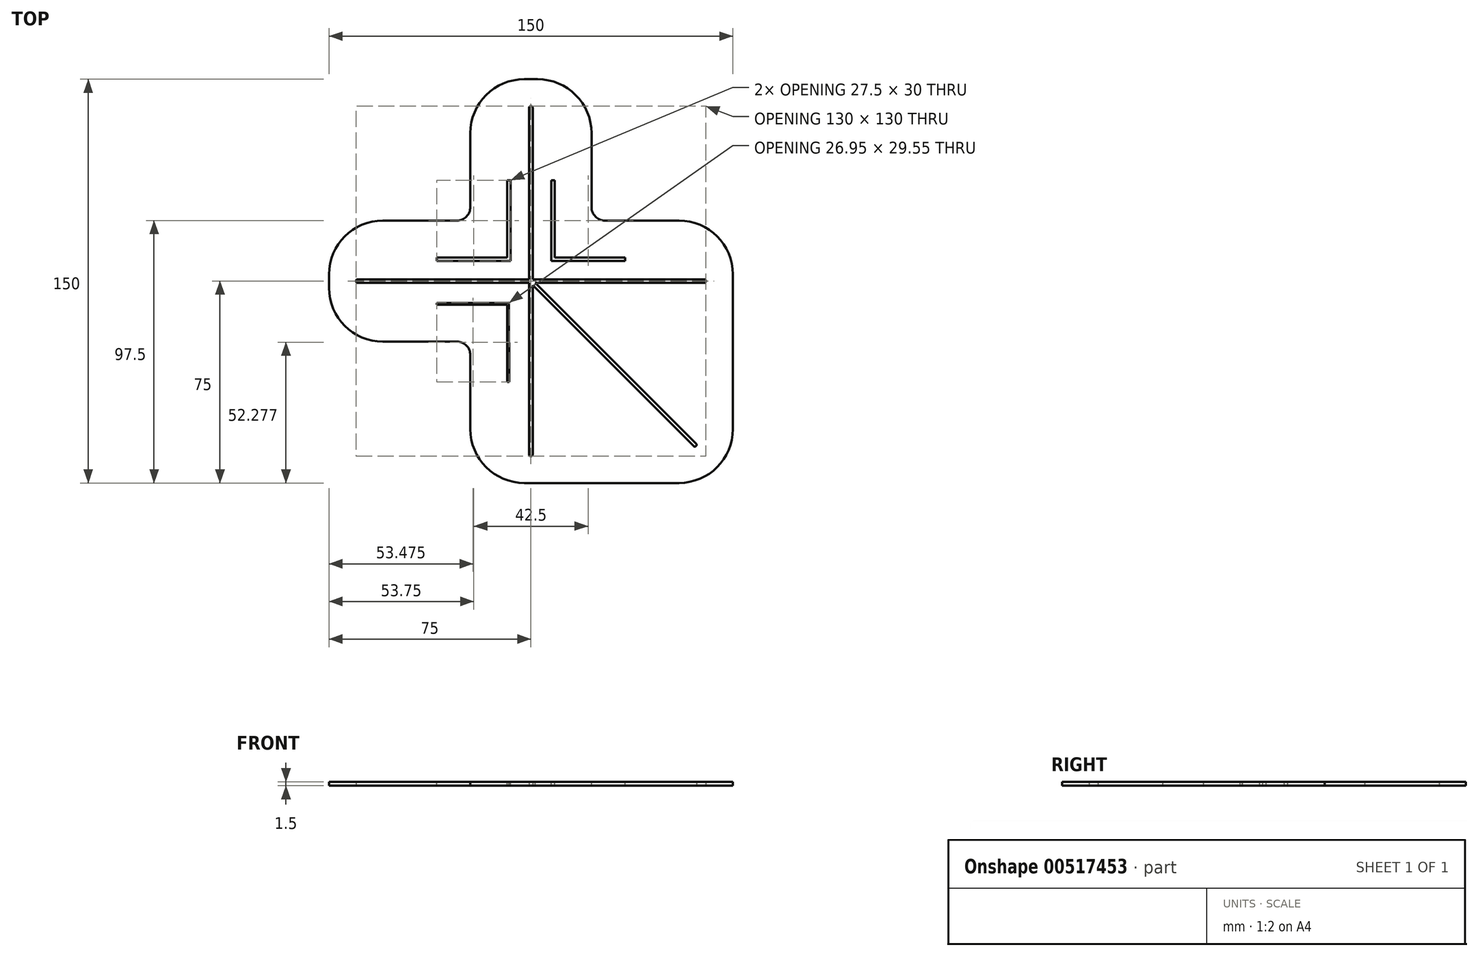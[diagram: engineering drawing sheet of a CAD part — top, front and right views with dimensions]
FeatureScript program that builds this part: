
annotation { "Feature Type Name" : "Feature", "Feature Type Description" : "" }
export const myFeature = defineFeature(function(context is Context, id is Id, definition is map)
    precondition{}
    {
        {
            var Q0;
            Q0=qCreatedBy(makeId("Top.planeOp"),FACE);
            var sketch = newSketch(context, id + "F0", { "sketchPlane" : qUnion([Q0])});
            skLineSegment(sketch, "E0.bottom", {"start": v(75, 75) * mm, "end": v(-75, 75) * mm});
            skLineSegment(sketch, "E0.top", {"start": v(75, -75) * mm, "end": v(-75, -75) * mm});
            skLineSegment(sketch, "E0.left", {"start": v(75, 75) * mm, "end": v(75, -75) * mm});
            skLineSegment(sketch, "E0.right", {"start": v(-75, 75) * mm, "end": v(-75, -75) * mm});
            skPoint(sketch, "E0.middle", {"position": v(0, 0) * mm});
            skLineSegment(sketch, "E1.bottom", {"start": v(0.65, -65) * mm, "end": v(-0.65, -65) * mm});
            skLineSegment(sketch, "E1.top", {"start": v(0.65, 65) * mm, "end": v(-0.65, 65) * mm});
            skLineSegment(sketch, "E1.left", {"start": v(0.65, -65) * mm, "end": v(0.65, -0.65) * mm});
            skLineSegment(sketch, "E1.right", {"start": v(-0.65, -65) * mm, "end": v(-0.65, -0.65) * mm});
            skLineSegment(sketch, "E2.bottom", {"start": v(-65, -0.65) * mm, "end": v(-0.65, -0.65) * mm});
            skLineSegment(sketch, "E2.top", {"start": v(-65, 0.65) * mm, "end": v(-0.65, 0.65) * mm});
            skLineSegment(sketch, "E2.left", {"start": v(-65, -0.65) * mm, "end": v(-65, 0.65) * mm});
            skLineSegment(sketch, "E2.right", {"start": v(65, -0.65) * mm, "end": v(65, 0.65) * mm});
            skLineSegment(sketch, "E3.trimOffspring", {"start": v(0.65, 0.65) * mm, "end": v(0.65, 65) * mm});
            skLineSegment(sketch, "E4.trimOffspring", {"start": v(0.65, 0.65) * mm, "end": v(65, 0.65) * mm});
            skLineSegment(sketch, "E5.trimOffspring", {"start": v(-0.65, 0.65) * mm, "end": v(-0.65, 65) * mm});
            skLineSegment(sketch, "E6.trimOffspring", {"start": v(0.65, -0.65) * mm, "end": v(65, -0.65) * mm});
            skSolve(sketch);
        }
        {
            var Q0;
            Q0 = qSketchRegion(id + "F0", true);
            extrude(context, id + "F1", {"entities" : qUnion([Q0]), "depth" : 1.5 * mm, "offsetDistance" : 25 * mm});
        }
        {
            var Q0;
            Q0=makeQuery(id+"F1.opExtrude","CAP_FACE",FACE,{"disambiguationData":[OSD([sQuery(id+"F0.wireOp",EDGE,"E0.bottom"),sQuery(id+"F0.wireOp",EDGE,"E0.top"),sQuery(id+"F0.wireOp",EDGE,"E0.left"),sQuery(id+"F0.wireOp",EDGE,"E0.right"),sQuery(id+"F0.wireOp",EDGE,"E1.bottom"),sQuery(id+"F0.wireOp",EDGE,"E1.top"),sQuery(id+"F0.wireOp",EDGE,"E1.left"),sQuery(id+"F0.wireOp",EDGE,"E1.right"),sQuery(id+"F0.wireOp",EDGE,"E2.bottom"),sQuery(id+"F0.wireOp",EDGE,"E2.top"),sQuery(id+"F0.wireOp",EDGE,"E2.left"),sQuery(id+"F0.wireOp",EDGE,"E2.right"),sQuery(id+"F0.wireOp",EDGE,"E3.trimOffspring"),sQuery(id+"F0.wireOp",EDGE,"E4.trimOffspring"),sQuery(id+"F0.wireOp",EDGE,"E5.trimOffspring"),sQuery(id+"F0.wireOp",EDGE,"E6.trimOffspring")])],"isStart":false});
            var sketch = newSketch(context, id + "F2", { "sketchPlane" : qUnion([Q0])});
            skLineSegment(sketch, "E7.0", {"start": v(0.46, 0.46) * mm, "end": v(61.74, -60.82) * mm});
            skLineSegment(sketch, "E8.0", {"start": v(-0.46, -0.46) * mm, "end": v(60.82, -61.74) * mm});
            skLineSegment(sketch, "E9", {"start": v(0.46, 0.46) * mm, "end": v(-0.46, -0.46) * mm});
            skLineSegment(sketch, "E10", {"start": v(61.74, -60.82) * mm, "end": v(60.82, -61.74) * mm});
            skSolve(sketch);
        }
        {
            var Q0;
            Q0 = qSketchRegion(id + "F2", true);
            extrude(context, id + "F3", {"entities" : qUnion([Q0]), "operationType" : NewBodyOperationType.REMOVE, "oppositeDirection" : true, "depth" : 25 * mm, "offsetDistance" : 25 * mm});
        }
        {
            var Q0;
            Q0=makeQuery(id+"F1.opExtrude","SWEPT_EDGE",EDGE,{"disambiguationData":[OSD([sQuery(id+"F0.wireOp",EDGE,"E1.bottom"),sQuery(id+"F0.wireOp",EDGE,"E1.left")])]});
            var Q1;
            Q1=makeQuery(id+"F1.opExtrude","SWEPT_EDGE",EDGE,{"disambiguationData":[OSD([sQuery(id+"F0.wireOp",EDGE,"E1.bottom"),sQuery(id+"F0.wireOp",EDGE,"E1.right")])]});
            var Q2;
            Q2=makeQuery(id+"F3.boolean.opBoolean","COPY",EDGE,{"derivedFrom":makeQuery(id+"F3.opExtrude","SWEPT_EDGE",EDGE,{"disambiguationData":[OSD([sQuery(id+"F2.wireOp",EDGE,"E8.0"),sQuery(id+"F2.wireOp",EDGE,"E10")])]})});
            var Q3;
            Q3=makeQuery(id+"F3.boolean.opBoolean","COPY",EDGE,{"derivedFrom":makeQuery(id+"F3.opExtrude","SWEPT_EDGE",EDGE,{"disambiguationData":[OSD([sQuery(id+"F2.wireOp",EDGE,"E7.0"),sQuery(id+"F2.wireOp",EDGE,"E10")])]})});
            var Q4;
            Q4=makeQuery(id+"F1.opExtrude","SWEPT_EDGE",EDGE,{"disambiguationData":[OSD([sQuery(id+"F0.wireOp",EDGE,"E2.right"),sQuery(id+"F0.wireOp",EDGE,"E4.trimOffspring")])]});
            var Q5;
            Q5=makeQuery(id+"F1.opExtrude","SWEPT_EDGE",EDGE,{"disambiguationData":[OSD([sQuery(id+"F0.wireOp",EDGE,"E2.right"),sQuery(id+"F0.wireOp",EDGE,"E6.trimOffspring")])]});
            var Q6;
            Q6=makeQuery(id+"F1.opExtrude","SWEPT_EDGE",EDGE,{"disambiguationData":[OSD([sQuery(id+"F0.wireOp",EDGE,"E2.bottom"),sQuery(id+"F0.wireOp",EDGE,"E2.left")])]});
            var Q7;
            Q7=makeQuery(id+"F1.opExtrude","SWEPT_EDGE",EDGE,{"disambiguationData":[OSD([sQuery(id+"F0.wireOp",EDGE,"E2.top"),sQuery(id+"F0.wireOp",EDGE,"E2.left")])]});
            var Q8;
            Q8=makeQuery(id+"F1.opExtrude","SWEPT_EDGE",EDGE,{"disambiguationData":[OSD([sQuery(id+"F0.wireOp",EDGE,"E1.top"),sQuery(id+"F0.wireOp",EDGE,"E5.trimOffspring")])]});
            var Q9;
            Q9=makeQuery(id+"F1.opExtrude","SWEPT_EDGE",EDGE,{"disambiguationData":[OSD([sQuery(id+"F0.wireOp",EDGE,"E1.top"),sQuery(id+"F0.wireOp",EDGE,"E3.trimOffspring")])]});
            fillet(context, id + "F4", {"entities" : qUnion([Q0, Q1, Q2, Q3, Q4, Q5, Q6, Q7, Q8, Q9]), "radius" : .5 * mm, "tangentPropagation" : true, "allowEdgeOverflow" : false});
        }
        {
            var Q0;
            Q0=makeQuery(id+"F1.opExtrude","CAP_FACE",FACE,{"disambiguationData":[OSD([sQuery(id+"F0.wireOp",EDGE,"E0.bottom"),sQuery(id+"F0.wireOp",EDGE,"E0.top"),sQuery(id+"F0.wireOp",EDGE,"E0.left"),sQuery(id+"F0.wireOp",EDGE,"E0.right"),sQuery(id+"F0.wireOp",EDGE,"E1.bottom"),sQuery(id+"F0.wireOp",EDGE,"E1.top"),sQuery(id+"F0.wireOp",EDGE,"E1.left"),sQuery(id+"F0.wireOp",EDGE,"E1.right"),sQuery(id+"F0.wireOp",EDGE,"E2.bottom"),sQuery(id+"F0.wireOp",EDGE,"E2.top"),sQuery(id+"F0.wireOp",EDGE,"E2.left"),sQuery(id+"F0.wireOp",EDGE,"E2.right"),sQuery(id+"F0.wireOp",EDGE,"E3.trimOffspring"),sQuery(id+"F0.wireOp",EDGE,"E4.trimOffspring"),sQuery(id+"F0.wireOp",EDGE,"E5.trimOffspring"),sQuery(id+"F0.wireOp",EDGE,"E6.trimOffspring")])],"isStart":false});
            var sketch = newSketch(context, id + "F5", { "sketchPlane" : qUnion([Q0])});
            skLineSegment(sketch, "E11.bottom", {"start": v(-7.5, 7.5) * mm, "end": v(7.5, 7.5) * mm, "construction": true});
            skLineSegment(sketch, "E11.top", {"start": v(-7.5, -7.5) * mm, "end": v(7.5, -7.5) * mm, "construction": true});
            skLineSegment(sketch, "E11.left", {"start": v(-7.5, 7.5) * mm, "end": v(-7.5, -7.5) * mm, "construction": true});
            skLineSegment(sketch, "E11.right", {"start": v(7.5, 7.5) * mm, "end": v(7.5, -7.5) * mm, "construction": true});
            skPoint(sketch, "E11.middle", {"position": v(0, 0) * mm});
            skLineSegment(sketch, "E12.top", {"start": v(-7.5, 37.5) * mm, "end": v(-8.6, 37.5) * mm});
            skLineSegment(sketch, "E12.left", {"start": v(-7.5, 7.5) * mm, "end": v(-7.5, 37.5) * mm});
            skLineSegment(sketch, "E12.right", {"start": v(-8.6, 8.6) * mm, "end": v(-8.6, 37.5) * mm});
            skLineSegment(sketch, "E13.bottom", {"start": v(-8.6, 7.5) * mm, "end": v(-35, 7.5) * mm});
            skLineSegment(sketch, "E13.top", {"start": v(-8.6, 8.6) * mm, "end": v(-35, 8.6) * mm});
            skLineSegment(sketch, "E13.right", {"start": v(-35, 7.5) * mm, "end": v(-35, 8.6) * mm});
            skCircle(sketch, "E14", {"center": v(0, 0) * mm, "radius": 18.96 * mm, "construction": true});
            skLineSegment(sketch, "E15", {"start": v(-8.6, 7.5) * mm, "end": v(-7.5, 7.5) * mm});
            skPoint(sketch, "E16.center", {"position": v(0, 8.75) * mm});
            skLineSegment(sketch, "E17", {"start": v(0, 75) * mm, "end": v(0, -60.5) * mm, "construction": true});
            skLineSegment(sketch, "E18", {"start": v(75, 0.15) * mm, "end": v(37.58, 0) * mm, "construction": true});
            skLineSegment(sketch, "E19.MirrorCS", {"start": v(8.6, 7.5) * mm, "end": v(7.5, 7.5) * mm});
            skLineSegment(sketch, "E20.MirrorCS", {"start": v(7.5, 37.5) * mm, "end": v(8.6, 37.5) * mm});
            skLineSegment(sketch, "E21.MirrorCS", {"start": v(35, 7.5) * mm, "end": v(35, 8.6) * mm});
            skLineSegment(sketch, "E22.MirrorCS", {"start": v(8.6, 8.6) * mm, "end": v(8.6, 37.5) * mm});
            skLineSegment(sketch, "E23.MirrorCS", {"start": v(8.6, 7.5) * mm, "end": v(35, 7.5) * mm});
            skLineSegment(sketch, "E24.MirrorCS", {"start": v(7.5, 7.5) * mm, "end": v(7.5, 37.5) * mm});
            skLineSegment(sketch, "E25.MirrorCS", {"start": v(8.6, 8.6) * mm, "end": v(35, 8.6) * mm});
            skLineSegment(sketch, "E26.MirrorCS", {"start": v(7.5, 7.5) * mm, "end": v(-7.5, 7.5) * mm, "construction": true});
            skSolve(sketch);
        }
        {
            var Q0;
            Q0 = qSketchRegion(id + "F5", true);
            extrude(context, id + "F6", {"entities" : qUnion([Q0]), "operationType" : NewBodyOperationType.REMOVE, "oppositeDirection" : true, "depth" : 25 * mm, "offsetDistance" : 25 * mm});
        }
        {
            var Q0;
            Q0=makeQuery(id+"F1.opExtrude","CAP_FACE",FACE,{"disambiguationData":[OSD([sQuery(id+"F0.wireOp",EDGE,"E0.bottom"),sQuery(id+"F0.wireOp",EDGE,"E0.top"),sQuery(id+"F0.wireOp",EDGE,"E0.left"),sQuery(id+"F0.wireOp",EDGE,"E0.right"),sQuery(id+"F0.wireOp",EDGE,"E1.bottom"),sQuery(id+"F0.wireOp",EDGE,"E1.top"),sQuery(id+"F0.wireOp",EDGE,"E1.left"),sQuery(id+"F0.wireOp",EDGE,"E1.right"),sQuery(id+"F0.wireOp",EDGE,"E2.bottom"),sQuery(id+"F0.wireOp",EDGE,"E2.top"),sQuery(id+"F0.wireOp",EDGE,"E2.left"),sQuery(id+"F0.wireOp",EDGE,"E2.right"),sQuery(id+"F0.wireOp",EDGE,"E3.trimOffspring"),sQuery(id+"F0.wireOp",EDGE,"E4.trimOffspring"),sQuery(id+"F0.wireOp",EDGE,"E5.trimOffspring"),sQuery(id+"F0.wireOp",EDGE,"E6.trimOffspring")])],"isStart":false});
            var sketch = newSketch(context, id + "F7", { "sketchPlane" : qUnion([Q0])});
            skLineSegment(sketch, "E27.bottom", {"start": v(-22.5, -22.5) * mm, "end": v(-127.5, -22.5) * mm});
            skLineSegment(sketch, "E27.top", {"start": v(-22.5, -127.5) * mm, "end": v(-127.5, -127.5) * mm});
            skLineSegment(sketch, "E27.left", {"start": v(-22.5, -22.5) * mm, "end": v(-22.5, -127.5) * mm});
            skLineSegment(sketch, "E27.right", {"start": v(-127.5, -22.5) * mm, "end": v(-127.5, -127.5) * mm});
            skPoint(sketch, "E27.middle", {"position": v(-75, -75) * mm});
            skLineSegment(sketch, "E28.bottom", {"start": v(-22.5, 22.5) * mm, "end": v(-127.5, 22.5) * mm});
            skLineSegment(sketch, "E28.top", {"start": v(-22.5, 127.5) * mm, "end": v(-127.5, 127.5) * mm});
            skLineSegment(sketch, "E28.left", {"start": v(-22.5, 22.5) * mm, "end": v(-22.5, 127.5) * mm});
            skLineSegment(sketch, "E28.right", {"start": v(-127.5, 22.5) * mm, "end": v(-127.5, 127.5) * mm});
            skPoint(sketch, "E28.middle", {"position": v(-75, 75) * mm});
            skLineSegment(sketch, "E29.bottom", {"start": v(22.5, 22.5) * mm, "end": v(127.5, 22.5) * mm});
            skLineSegment(sketch, "E29.top", {"start": v(22.5, 127.5) * mm, "end": v(127.5, 127.5) * mm});
            skLineSegment(sketch, "E29.left", {"start": v(22.5, 22.5) * mm, "end": v(22.5, 127.5) * mm});
            skLineSegment(sketch, "E29.right", {"start": v(127.5, 22.5) * mm, "end": v(127.5, 127.5) * mm});
            skPoint(sketch, "E29.middle", {"position": v(75, 75) * mm});
            skSolve(sketch);
        }
        {
            var Q0;
            Q0 = qSketchRegion(id + "F7", true);
            extrude(context, id + "F8", {"entities" : qUnion([Q0]), "operationType" : NewBodyOperationType.REMOVE, "oppositeDirection" : true, "depth" : 25 * mm, "offsetDistance" : 25 * mm});
        }
        {
            var Q0;
            Q0=makeQuery(id+"F8.boolean.opBoolean","INTERSECT",EDGE,{"derivedFrom":[makeQuery(id+"F1.opExtrude","SWEPT_FACE",FACE,{"disambiguationData":[OSD([sQuery(id+"F0.wireOp",EDGE,"E0.right")])]}),makeQuery(id+"F8.opExtrude","SWEPT_FACE",FACE,{"disambiguationData":[OSD([sQuery(id+"F7.wireOp",EDGE,"E27.bottom")])]})]});
            var Q1;
            Q1=makeQuery(id+"F8.boolean.opBoolean","INTERSECT",EDGE,{"derivedFrom":[makeQuery(id+"F1.opExtrude","SWEPT_FACE",FACE,{"disambiguationData":[OSD([sQuery(id+"F0.wireOp",EDGE,"E0.top")])]}),makeQuery(id+"F8.opExtrude","SWEPT_FACE",FACE,{"disambiguationData":[OSD([sQuery(id+"F7.wireOp",EDGE,"E27.left")])]})]});
            var Q2;
            Q2=makeQuery(id+"F1.opExtrude","SWEPT_EDGE",EDGE,{"disambiguationData":[OSD([sQuery(id+"F0.wireOp",EDGE,"E0.top"),sQuery(id+"F0.wireOp",EDGE,"E0.left")])]});
            var Q3;
            Q3=makeQuery(id+"F8.boolean.opBoolean","INTERSECT",EDGE,{"derivedFrom":[makeQuery(id+"F1.opExtrude","SWEPT_FACE",FACE,{"disambiguationData":[OSD([sQuery(id+"F0.wireOp",EDGE,"E0.left")])]}),makeQuery(id+"F8.opExtrude","SWEPT_FACE",FACE,{"disambiguationData":[OSD([sQuery(id+"F7.wireOp",EDGE,"E29.bottom")])]})]});
            var Q4;
            Q4=makeQuery(id+"F8.boolean.opBoolean","INTERSECT",EDGE,{"derivedFrom":[makeQuery(id+"F1.opExtrude","SWEPT_FACE",FACE,{"disambiguationData":[OSD([sQuery(id+"F0.wireOp",EDGE,"E0.bottom")])]}),makeQuery(id+"F8.opExtrude","SWEPT_FACE",FACE,{"disambiguationData":[OSD([sQuery(id+"F7.wireOp",EDGE,"E29.left")])]})]});
            var Q5;
            Q5=makeQuery(id+"F8.boolean.opBoolean","INTERSECT",EDGE,{"derivedFrom":[makeQuery(id+"F1.opExtrude","SWEPT_FACE",FACE,{"disambiguationData":[OSD([sQuery(id+"F0.wireOp",EDGE,"E0.bottom")])]}),makeQuery(id+"F8.opExtrude","SWEPT_FACE",FACE,{"disambiguationData":[OSD([sQuery(id+"F7.wireOp",EDGE,"E28.left")])]})]});
            var Q6;
            Q6=makeQuery(id+"F8.boolean.opBoolean","INTERSECT",EDGE,{"derivedFrom":[makeQuery(id+"F1.opExtrude","SWEPT_FACE",FACE,{"disambiguationData":[OSD([sQuery(id+"F0.wireOp",EDGE,"E0.right")])]}),makeQuery(id+"F8.opExtrude","SWEPT_FACE",FACE,{"disambiguationData":[OSD([sQuery(id+"F7.wireOp",EDGE,"E28.bottom")])]})]});
            fillet(context, id + "F9", {"entities" : qUnion([Q0, Q1, Q2, Q3, Q4, Q5, Q6]), "radius" : 20 * mm, "tangentPropagation" : true, "allowEdgeOverflow" : false});
        }
        {
            var Q0;
            Q0=makeQuery(id+"F8.boolean.opBoolean","COPY",EDGE,{"derivedFrom":makeQuery(id+"F8.opExtrude","SWEPT_EDGE",EDGE,{"disambiguationData":[OSD([sQuery(id+"F7.wireOp",EDGE,"E27.bottom"),sQuery(id+"F7.wireOp",EDGE,"E27.left")])]})});
            var Q1;
            Q1=makeQuery(id+"F8.boolean.opBoolean","COPY",EDGE,{"derivedFrom":makeQuery(id+"F8.opExtrude","SWEPT_EDGE",EDGE,{"disambiguationData":[OSD([sQuery(id+"F7.wireOp",EDGE,"E28.bottom"),sQuery(id+"F7.wireOp",EDGE,"E28.left")])]})});
            var Q2;
            Q2=makeQuery(id+"F8.boolean.opBoolean","COPY",EDGE,{"derivedFrom":makeQuery(id+"F8.opExtrude","SWEPT_EDGE",EDGE,{"disambiguationData":[OSD([sQuery(id+"F7.wireOp",EDGE,"E29.bottom"),sQuery(id+"F7.wireOp",EDGE,"E29.left")])]})});
            fillet(context, id + "F10", {"entities" : qUnion([Q0, Q1, Q2]), "radius" : 5 * mm, "tangentPropagation" : true, "allowEdgeOverflow" : false});
        }
        {
            var Q0;
            Q0=makeQuery(id+"F1.opExtrude","CAP_FACE",FACE,{"disambiguationData":[OSD([sQuery(id+"F0.wireOp",EDGE,"E0.bottom"),sQuery(id+"F0.wireOp",EDGE,"E0.top"),sQuery(id+"F0.wireOp",EDGE,"E0.left"),sQuery(id+"F0.wireOp",EDGE,"E0.right"),sQuery(id+"F0.wireOp",EDGE,"E1.bottom"),sQuery(id+"F0.wireOp",EDGE,"E1.top"),sQuery(id+"F0.wireOp",EDGE,"E1.left"),sQuery(id+"F0.wireOp",EDGE,"E1.right"),sQuery(id+"F0.wireOp",EDGE,"E2.bottom"),sQuery(id+"F0.wireOp",EDGE,"E2.top"),sQuery(id+"F0.wireOp",EDGE,"E2.left"),sQuery(id+"F0.wireOp",EDGE,"E2.right"),sQuery(id+"F0.wireOp",EDGE,"E3.trimOffspring"),sQuery(id+"F0.wireOp",EDGE,"E4.trimOffspring"),sQuery(id+"F0.wireOp",EDGE,"E5.trimOffspring"),sQuery(id+"F0.wireOp",EDGE,"E6.trimOffspring")])],"isStart":false});
            var sketch = newSketch(context, id + "F11", { "sketchPlane" : qUnion([Q0])});
            skLineSegment(sketch, "E30", {"start": v(8.42, -7.5) * mm, "end": v(9.52, -8.6) * mm});
            skLineSegment(sketch, "E31", {"start": v(9.52, -8.6) * mm, "end": v(37.29, -9.78) * mm});
            skLineSegment(sketch, "E32", {"start": v(37.29, -9.78) * mm, "end": v(36.06, -4.77) * mm});
            skLineSegment(sketch, "E33", {"start": v(36.06, -4.77) * mm, "end": v(8.42, -7.5) * mm});
            skLineSegment(sketch, "E34", {"start": v(7.5, -8.42) * mm, "end": v(8.6, -9.52) * mm});
            skLineSegment(sketch, "E35", {"start": v(8.6, -9.52) * mm, "end": v(14.81, -40.76) * mm});
            skLineSegment(sketch, "E36", {"start": v(14.81, -40.76) * mm, "end": v(3.89, -40.76) * mm});
            skLineSegment(sketch, "E37", {"start": v(3.89, -40.76) * mm, "end": v(7.5, -8.42) * mm});
            skSolve(sketch);
        }
        {
            var Q0;
            Q0 = qSketchRegion(id + "F11", true);
            var Q1;
            Q1=makeQuery(id+"F1.opExtrude","CAP_FACE",FACE,{"disambiguationData":[OSD([sQuery(id+"F0.wireOp",EDGE,"E0.bottom"),sQuery(id+"F0.wireOp",EDGE,"E0.top"),sQuery(id+"F0.wireOp",EDGE,"E0.left"),sQuery(id+"F0.wireOp",EDGE,"E0.right"),sQuery(id+"F0.wireOp",EDGE,"E1.bottom"),sQuery(id+"F0.wireOp",EDGE,"E1.top"),sQuery(id+"F0.wireOp",EDGE,"E1.left"),sQuery(id+"F0.wireOp",EDGE,"E1.right"),sQuery(id+"F0.wireOp",EDGE,"E2.bottom"),sQuery(id+"F0.wireOp",EDGE,"E2.top"),sQuery(id+"F0.wireOp",EDGE,"E2.left"),sQuery(id+"F0.wireOp",EDGE,"E2.right"),sQuery(id+"F0.wireOp",EDGE,"E3.trimOffspring"),sQuery(id+"F0.wireOp",EDGE,"E4.trimOffspring"),sQuery(id+"F0.wireOp",EDGE,"E5.trimOffspring"),sQuery(id+"F0.wireOp",EDGE,"E6.trimOffspring")])],"isStart":true});
            extrude(context, id + "F12", {"entities" : qUnion([Q0]), "operationType" : NewBodyOperationType.ADD, "endBound" : BoundingType.UP_TO_SURFACE, "oppositeDirection" : true, "depth" : 15 * mm, "endBoundEntityFace" : qUnion([Q1]), "offsetDistance" : 25 * mm});
        }
        {
            var Q0;
            Q0=makeQuery(id+"F12.boolean.opBoolean","MERGE",FACE,{"derivedFrom":[makeQuery(id+"F1.opExtrude","CAP_FACE",FACE,{"disambiguationData":[OSD([sQuery(id+"F0.wireOp",EDGE,"E0.bottom"),sQuery(id+"F0.wireOp",EDGE,"E0.top"),sQuery(id+"F0.wireOp",EDGE,"E0.left"),sQuery(id+"F0.wireOp",EDGE,"E0.right"),sQuery(id+"F0.wireOp",EDGE,"E1.bottom"),sQuery(id+"F0.wireOp",EDGE,"E1.top"),sQuery(id+"F0.wireOp",EDGE,"E1.left"),sQuery(id+"F0.wireOp",EDGE,"E1.right"),sQuery(id+"F0.wireOp",EDGE,"E2.bottom"),sQuery(id+"F0.wireOp",EDGE,"E2.top"),sQuery(id+"F0.wireOp",EDGE,"E2.left"),sQuery(id+"F0.wireOp",EDGE,"E2.right"),sQuery(id+"F0.wireOp",EDGE,"E3.trimOffspring"),sQuery(id+"F0.wireOp",EDGE,"E4.trimOffspring"),sQuery(id+"F0.wireOp",EDGE,"E5.trimOffspring"),sQuery(id+"F0.wireOp",EDGE,"E6.trimOffspring")])],"isStart":false}),makeQuery(id+"F12.opExtrude","CAP_FACE",FACE,{"disambiguationData":[OSD([sQuery(id+"F11.wireOp",EDGE,"E30"),sQuery(id+"F11.wireOp",EDGE,"E31"),sQuery(id+"F11.wireOp",EDGE,"E32"),sQuery(id+"F11.wireOp",EDGE,"E33")])],"isStart":true}),makeQuery(id+"F12.opExtrude","CAP_FACE",FACE,{"disambiguationData":[OSD([sQuery(id+"F11.wireOp",EDGE,"E34"),sQuery(id+"F11.wireOp",EDGE,"E35"),sQuery(id+"F11.wireOp",EDGE,"E36"),sQuery(id+"F11.wireOp",EDGE,"E37")])],"isStart":true})]});
            var sketch = newSketch(context, id + "F13", { "sketchPlane" : qUnion([Q0])});
            skLineSegment(sketch, "E38.0", {"start": v(-8.8, 8.8) * mm, "end": v(-8.8, 37.5) * mm});
            skLineSegment(sketch, "E39.0", {"start": v(-8.8, 8.8) * mm, "end": v(-35, 8.8) * mm});
            skLineSegment(sketch, "E40", {"start": v(-8.8, 37.5) * mm, "end": v(-8.05, 37.5) * mm});
            skLineSegment(sketch, "E41", {"start": v(-8.05, 37.5) * mm, "end": v(-8.24, 7.95) * mm});
            skLineSegment(sketch, "E42", {"start": v(-8.24, 7.95) * mm, "end": v(-35, 8.11) * mm});
            skLineSegment(sketch, "E43", {"start": v(-35, 8.11) * mm, "end": v(-35, 8.8) * mm});
            skLineSegment(sketch, "E44", {"start": v(0, 0) * mm, "end": v(0, 20.13) * mm, "construction": true});
            skLineSegment(sketch, "E45", {"start": v(-23.85, 0) * mm, "end": v(0, 0) * mm, "construction": true});
            skLineSegment(sketch, "E46.MirrorCS", {"start": v(8.8, 37.5) * mm, "end": v(8.05, 37.5) * mm});
            skLineSegment(sketch, "E47.MirrorCS", {"start": v(35, 8.11) * mm, "end": v(35, 8.8) * mm});
            skLineSegment(sketch, "E48.MirrorCS", {"start": v(8.8, 8.8) * mm, "end": v(8.8, 37.5) * mm});
            skLineSegment(sketch, "E49.MirrorCS", {"start": v(8.24, 7.95) * mm, "end": v(35, 8.11) * mm});
            skLineSegment(sketch, "E50.MirrorCS", {"start": v(8.05, 37.5) * mm, "end": v(8.24, 7.95) * mm});
            skLineSegment(sketch, "E51.MirrorCS", {"start": v(8.8, 8.8) * mm, "end": v(35, 8.8) * mm});
            skLineSegment(sketch, "E52.MirrorCS", {"start": v(-35, -8.11) * mm, "end": v(-35, -8.8) * mm});
            skLineSegment(sketch, "E53.MirrorCS", {"start": v(-8.8, -37.5) * mm, "end": v(-8.05, -37.5) * mm});
            skLineSegment(sketch, "E54.MirrorCS", {"start": v(-8.8, -8.8) * mm, "end": v(-8.8, -37.5) * mm});
            skLineSegment(sketch, "E55.MirrorCS", {"start": v(-8.8, -8.8) * mm, "end": v(-35, -8.8) * mm});
            skLineSegment(sketch, "E56.MirrorCS", {"start": v(-8.24, -7.95) * mm, "end": v(-35, -8.11) * mm});
            skLineSegment(sketch, "E57.MirrorCS", {"start": v(-8.05, -37.5) * mm, "end": v(-8.24, -7.95) * mm});
            skSolve(sketch);
        }
        {
            var Q0;
            Q0 = qSketchRegion(id + "F13", true);
            extrude(context, id + "F14", {"entities" : qUnion([Q0]), "operationType" : NewBodyOperationType.REMOVE, "oppositeDirection" : true, "depth" : 25 * mm, "offsetDistance" : 25 * mm});
        }
    });
